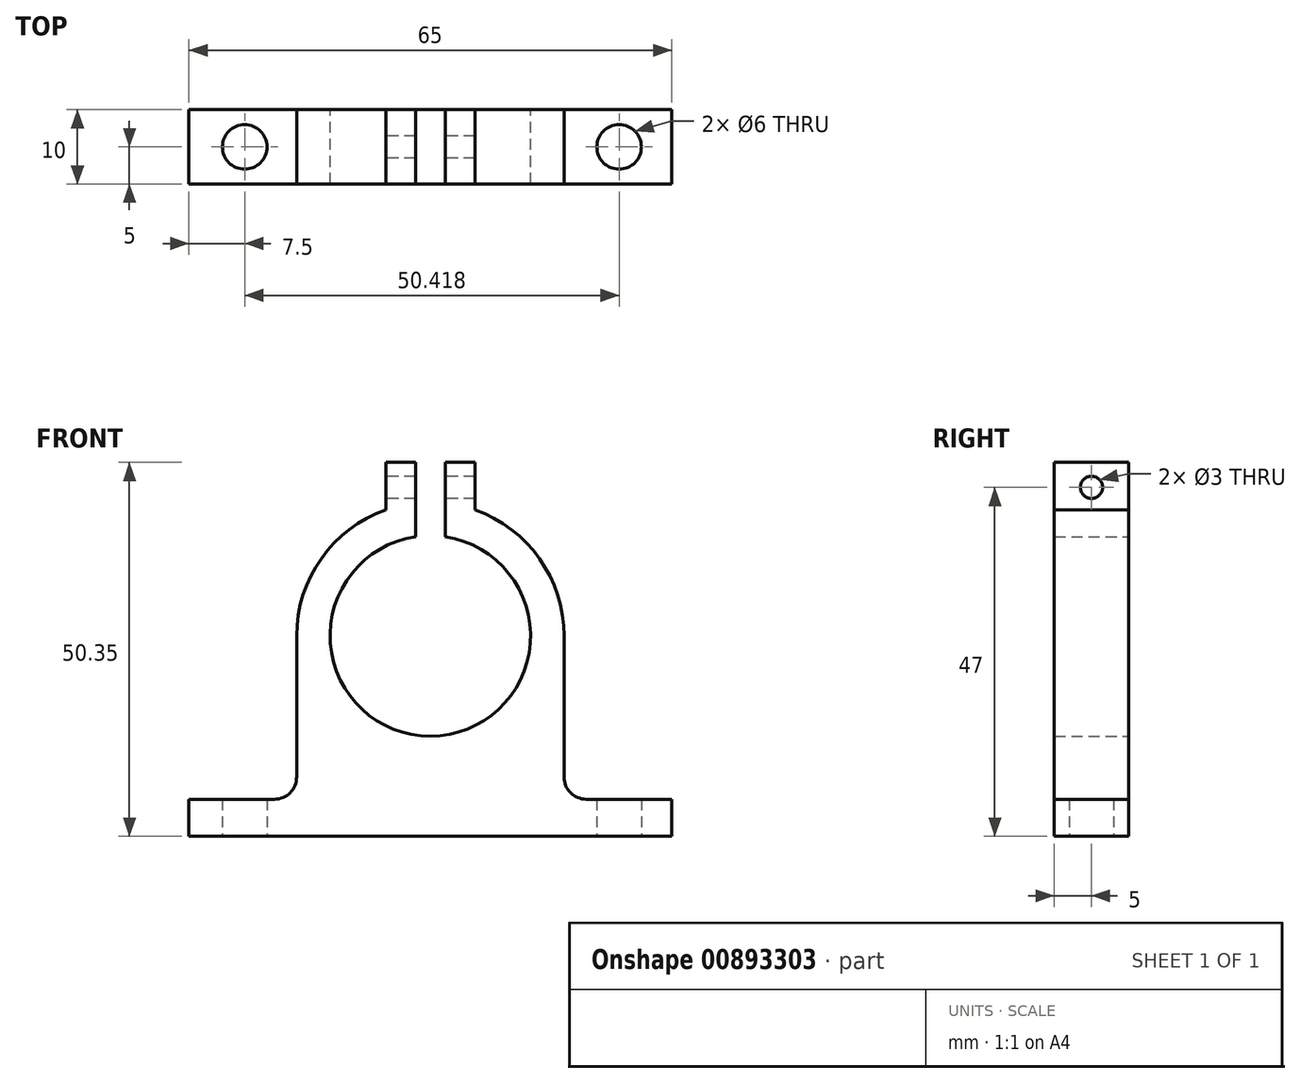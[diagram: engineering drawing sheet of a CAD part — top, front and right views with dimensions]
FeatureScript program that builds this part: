
annotation { "Feature Type Name" : "Feature", "Feature Type Description" : "" }
export const myFeature = defineFeature(function(context is Context, id is Id, definition is map)
    precondition{}
    {
        {
            var Q0;
            Q0=qCreatedBy(makeId("Front.planeOp"),FACE);
            var sketch = newSketch(context, id + "F0", { "sketchPlane" : qUnion([Q0])});
            skPoint(sketch, "E0", {"position": v(0, 27) * mm});
            skArc(sketch, "E1", {"start": v(-2, 40.35) * mm, "mid": v(0, 13.5) * mm, "end": v(2, 40.35) * mm});
            skLineSegment(sketch, "E2.top", {"start": v(-15, 0) * mm, "end": v(15, 0) * mm});
            skPoint(sketch, "E3", {"position": v(-25, 0) * mm});
            skPoint(sketch, "E4", {"position": v(25, 0) * mm});
            skPoint(sketch, "E5", {"position": v(-32.5, 0) * mm});
            skLineSegment(sketch, "E6.bottom", {"start": v(-32.5, 0) * mm, "end": v(32.5, 0) * mm});
            skLineSegment(sketch, "E6.top", {"start": v(-32.5, 5) * mm, "end": v(-18, 5) * mm});
            skLineSegment(sketch, "E6.left", {"start": v(-32.5, 0) * mm, "end": v(-32.5, 5) * mm});
            skLineSegment(sketch, "E6.right", {"start": v(32.5, 0) * mm, "end": v(32.5, 5) * mm});
            skLineSegment(sketch, "E7.trimOffspring", {"start": v(18, 5) * mm, "end": v(32.5, 5) * mm});
            skLineSegment(sketch, "E8", {"start": v(0, 0) * mm, "end": v(0, 63.32) * mm, "construction": true});
            skLineSegment(sketch, "E9.0", {"start": v(2, 40.35) * mm, "end": v(2, 50.35) * mm});
            skLineSegment(sketch, "E10.0", {"start": v(-2, 40.35) * mm, "end": v(-2, 50.35) * mm});
            skLineSegment(sketch, "E11.0", {"start": v(18, 5) * mm, "end": v(18, 27) * mm});
            skLineSegment(sketch, "E12.0", {"start": v(-18, 5) * mm, "end": v(-18, 27) * mm});
            skArc(sketch, "E13.trimOffspring", {"start": v(18, 27) * mm, "mid": v(14.7, 37.4) * mm, "end": v(6, 43.97) * mm});
            skArc(sketch, "E14.trimOffspring", {"start": v(-6, 43.97) * mm, "mid": v(-14.7, 37.4) * mm, "end": v(-18, 27) * mm});
            skPoint(sketch, "E15", {"position": v(-2, 50.35) * mm});
            skPoint(sketch, "E16", {"position": v(2, 50.35) * mm});
            skLineSegment(sketch, "E17.left", {"start": v(-2, 50.35) * mm, "end": v(-2, 40.4) * mm});
            skLineSegment(sketch, "E18.0", {"start": v(-6, 50.35) * mm, "end": v(-6, 43.97) * mm});
            skLineSegment(sketch, "E19.0", {"start": v(6, 43.97) * mm, "end": v(6, 50.35) * mm});
            skLineSegment(sketch, "E20", {"start": v(-6, 50.35) * mm, "end": v(-2, 50.35) * mm});
            skLineSegment(sketch, "E21", {"start": v(2, 50.35) * mm, "end": v(6, 50.35) * mm});
            skSolve(sketch);
        }
        {
            var Q0;
            {var subQ2=sQuery(id+"F0.wireOp",EDGE,"E1");Q0=makeQuery(id+"F0.imprint","IMPRINT",FACE,{"disambiguationData":[TD([[makeQuery(id+"F0.imprint","IMPRINT",EDGE,{"derivedFrom":subQ2}),-1.0]])]});}
            extrude(context, id + "F1", {"entities" : qUnion([Q0]), "endBound" : BoundingType.SYMMETRIC, "depth" : 10 * mm, "offsetDistance" : 25 * mm});
        }
        {
            var Q0;
            Q0=qCreatedBy(makeId("Right.planeOp"),FACE);
            var sketch = newSketch(context, id + "F2", { "sketchPlane" : qUnion([Q0])});
            skCircle(sketch, "E22", {"center": v(0, 47) * mm, "radius": 1.5 * mm});
            skSolve(sketch);
        }
        {
            var Q0;
            Q0=makeQuery(id+"F2.imprint","IMPRINT",FACE,{"disambiguationData":[TD([[makeQuery(id+"F2.imprint","IMPRINT",EDGE,{"derivedFrom":sQuery(id+"F2.wireOp",EDGE,"E22")}),1.0]])]});
            extrude(context, id + "F3", {"entities" : qUnion([Q0]), "endBound" : BoundingType.SYMMETRIC, "depth" : 25 * mm, "offsetDistance" : 25 * mm});
        }
        {
            var Q0;
            Q0=makeQuery(id+"F3.opExtrude","SWEPT_BODY",BODY,{"disambiguationData":[OSD([sQuery(id+"F2.wireOp",EDGE,"E22")])]});
            var Q1;
            Q1=makeQuery(id+"F1.opExtrude","SWEPT_BODY",BODY,{"disambiguationData":[OSD([sQuery(id+"F0.wireOp",EDGE,"E1"),sQuery(id+"F0.wireOp",EDGE,"JRk5cEWa-95By-ki05-dz7P-2yXtRBB5Jr1I"),sQuery(id+"F0.wireOp",EDGE,"E2.left"),sQuery(id+"F0.wireOp",EDGE,"E2.right"),sQuery(id+"F0.wireOp",EDGE,"eb983c25-6e29-4b95-b699-ed41e249fcaf.trimOffspring"),sQuery(id+"F0.wireOp",EDGE,"ho1JlvTj-0JYC-gs2l-v9We-z4PGPtIeFMqr.top"),sQuery(id+"F0.wireOp",EDGE,"ho1JlvTj-0JYC-gs2l-v9We-z4PGPtIeFMqr.left"),sQuery(id+"F0.wireOp",EDGE,"ho1JlvTj-0JYC-gs2l-v9We-z4PGPtIeFMqr.right"),sQuery(id+"F0.wireOp",EDGE,"bpHtGYCb-EgVX-TDrV-v1JF-ow5r1IrcaxIA.top"),sQuery(id+"F0.wireOp",EDGE,"bpHtGYCb-EgVX-TDrV-v1JF-ow5r1IrcaxIA.left"),sQuery(id+"F0.wireOp",EDGE,"bpHtGYCb-EgVX-TDrV-v1JF-ow5r1IrcaxIA.right"),sQuery(id+"F0.wireOp",EDGE,"E6.bottom"),sQuery(id+"F0.wireOp",EDGE,"E6.top"),sQuery(id+"F0.wireOp",EDGE,"E6.left"),sQuery(id+"F0.wireOp",EDGE,"E6.right"),sQuery(id+"F0.wireOp",EDGE,"E7.trimOffspring")])]});
            booleanBodies(context, id + "F4", {"operationType" : BooleanOperationType.SUBTRACTION, "tools" : qUnion([Q0]), "targets" : qUnion([Q1])});
        }
        {
            var Q0;
            Q0=makeQuery(id+"F1.opExtrude","SWEPT_EDGE",EDGE,{"disambiguationData":[OSD([sQuery(id+"F0.wireOp",EDGE,"E7.trimOffspring"),sQuery(id+"F0.wireOp",EDGE,"E11.0")])]});
            var Q1;
            Q1=makeQuery(id+"F1.opExtrude","SWEPT_EDGE",EDGE,{"disambiguationData":[OSD([sQuery(id+"F0.wireOp",EDGE,"E6.top"),sQuery(id+"F0.wireOp",EDGE,"E12.0")])]});
            fillet(context, id + "F5", {"entities" : qUnion([Q0, Q1]), "radius" : 3 * mm, "tangentPropagation" : true, "allowEdgeOverflow" : false});
        }
        {
            var Q0;
            Q0=qCreatedBy(makeId("Top.planeOp"),FACE);
            var sketch = newSketch(context, id + "F6", { "sketchPlane" : qUnion([Q0])});
            skPoint(sketch, "E23", {"position": v(-25, 0) * mm});
            skPoint(sketch, "E24", {"position": v(25, 0) * mm});
            skCircle(sketch, "E25", {"center": v(-25, 0) * mm, "radius": 3 * mm});
            skCircle(sketch, "E26", {"center": v(25.42, 0) * mm, "radius": 3 * mm});
            skSolve(sketch);
        }
        {
            var Q0;
            Q0=makeQuery(id+"F6.imprint","IMPRINT",FACE,{"disambiguationData":[TD([[makeQuery(id+"F6.imprint","IMPRINT",EDGE,{"derivedFrom":sQuery(id+"F6.wireOp",EDGE,"E25")}),1.0]])]});
            var Q1;
            Q1=makeQuery(id+"F6.imprint","IMPRINT",FACE,{"disambiguationData":[TD([[makeQuery(id+"F6.imprint","IMPRINT",EDGE,{"derivedFrom":sQuery(id+"F6.wireOp",EDGE,"E26")}),1.0]])]});
            extrude(context, id + "F7", {"entities" : qUnion([Q0, Q1]), "depth" : 25 * mm, "offsetDistance" : 25 * mm});
        }
        {
            var Q0;
            Q0=makeQuery(id+"F7.opExtrude","SWEPT_BODY",BODY,{"disambiguationData":[OSD([sQuery(id+"F6.wireOp",EDGE,"E26")])]});
            var Q1;
            Q1=makeQuery(id+"F7.opExtrude","SWEPT_BODY",BODY,{"disambiguationData":[OSD([sQuery(id+"F6.wireOp",EDGE,"E25")])]});
            var Q2;
            Q2=makeQuery(id+"F1.opExtrude","SWEPT_BODY",BODY,{"disambiguationData":[OSD([sQuery(id+"F0.wireOp",EDGE,"E1"),sQuery(id+"F0.wireOp",EDGE,"JRk5cEWa-95By-ki05-dz7P-2yXtRBB5Jr1I"),sQuery(id+"F0.wireOp",EDGE,"E2.left"),sQuery(id+"F0.wireOp",EDGE,"E2.right"),sQuery(id+"F0.wireOp",EDGE,"eb983c25-6e29-4b95-b699-ed41e249fcaf.trimOffspring"),sQuery(id+"F0.wireOp",EDGE,"ho1JlvTj-0JYC-gs2l-v9We-z4PGPtIeFMqr.top"),sQuery(id+"F0.wireOp",EDGE,"ho1JlvTj-0JYC-gs2l-v9We-z4PGPtIeFMqr.left"),sQuery(id+"F0.wireOp",EDGE,"ho1JlvTj-0JYC-gs2l-v9We-z4PGPtIeFMqr.right"),sQuery(id+"F0.wireOp",EDGE,"bpHtGYCb-EgVX-TDrV-v1JF-ow5r1IrcaxIA.top"),sQuery(id+"F0.wireOp",EDGE,"bpHtGYCb-EgVX-TDrV-v1JF-ow5r1IrcaxIA.left"),sQuery(id+"F0.wireOp",EDGE,"bpHtGYCb-EgVX-TDrV-v1JF-ow5r1IrcaxIA.right"),sQuery(id+"F0.wireOp",EDGE,"E6.bottom"),sQuery(id+"F0.wireOp",EDGE,"E6.top"),sQuery(id+"F0.wireOp",EDGE,"E6.left"),sQuery(id+"F0.wireOp",EDGE,"E6.right"),sQuery(id+"F0.wireOp",EDGE,"E7.trimOffspring")])]});
            booleanBodies(context, id + "F8", {"operationType" : BooleanOperationType.SUBTRACTION, "tools" : qUnion([Q0, Q1]), "targets" : qUnion([Q2])});
        }
    });
